# Revit family: FF109 Vent Duct Fire Sleeve - Rectanglular
name_source: partatom
category: Specialty Equipment
revit_build: Autodesk Revit 2015 (Build: 20160512_0715(x64)
units: mm (PartAtom-declared; Revit-internal decimal feet)

## types (5) — shared parameters
Conduit Material Suitability = HDEP, UPVC, PVC,
Description = FireFly 109 Vent Duct Fire Sleeve
IFC Classification = Building Element Proxy
Manufacturer = Tenmat ltd
Material = Intumescent Sealant
Performance = BS EN 1366-3:2009 & BS 476, ETA-12/0332, 1224-CPR-0341, CE Marked
URL = https://www.tenmat.com
Youtube clip = https://www.youtube.com

## per-type parameters (varying)
| type | Height | Width |
| Duct size - 110 x 54 | 54 mm  [stored 0.177165 ft] | 110 mm  [stored 0.360892 ft] |
| Duct size - 204 x 60 | 60 mm | 204 mm |
| Duct size - 220 x 90 | 90 mm  [stored 0.295276 ft] | 220 mm |
| Duct size - 234 x 29 | 29 mm | 234 mm |
| Duct size - 308 x 29 | 29 mm | 308 mm |

note: [stored X ft] marks values corroborated as IEEE doubles in the binary element streams (Revit-internal decimal feet)

## geometry (parser evidence)
native form markers: Blend x2, Sweep x3
no freeform markers — native parametric forms only
